# Revit family: Ladder_Rung_Kattsafe_Vertical_FallArrest_ParapetPlatform
name_source: partatom
category: Specialty Equipment
units: mm (PartAtom-declared; Revit-internal decimal feet)

## family parameters
Always vertical = Yes
Cut with Voids When Loaded = No
Enable Cutting in Views = No
Maintain Annotation Orientation = No
OmniClass Number = 23.17.23.15
Part Type = Normal
Room Calculation Point = No
Round Connector Dimension = Use Diameter
Shared = No
Work Plane-Based = No

## types (1)
- RL52
    Assembly Code = E1090100
    Default Elevation = 0 mm  [stored 0 ft]
    Description = Vertical fall arrest ladder with guardrails, parapet platform and 1.0m landing – concrete mount. Available with metal deck and concrete floor mounting options
    ElementType = Ladder
    Export Type to IFC As = IfcBuildingElementProxy
    IfcExportAs = IfcBuildingElementProxy
    IfcExportType = USERDEFINED
    Manufacturer = Kattsafe®
    ManufacturerOverallWidth = 800 mm  [stored 2.62467 ft]
    ManufacturerSpecCode = RL52
    ManufacturerURLProductSpecific = https://kattsafe.com.au
    Material = Aluminum_Kattsafe_Satin
    Model = RL52
    ModifiedIssue = 20250224 $
    Type Comments = Ladder - Vertical - Rung - Fall Arrest - Parapet Platform
    Type IFC Predefined Type = USERDEFINED
    URL = https://kattsafe.com.au
    Uniclass2015Code = Pr_25_30_85_02
    Uniclass2015Title = Access ladders
    Uniclass2015Version = Products v1.35

note: [stored X ft] marks values corroborated as IEEE doubles in the binary element streams (Revit-internal decimal feet)

## geometry (parser evidence)
native form markers: Sweep x29
no freeform markers — native parametric forms only
